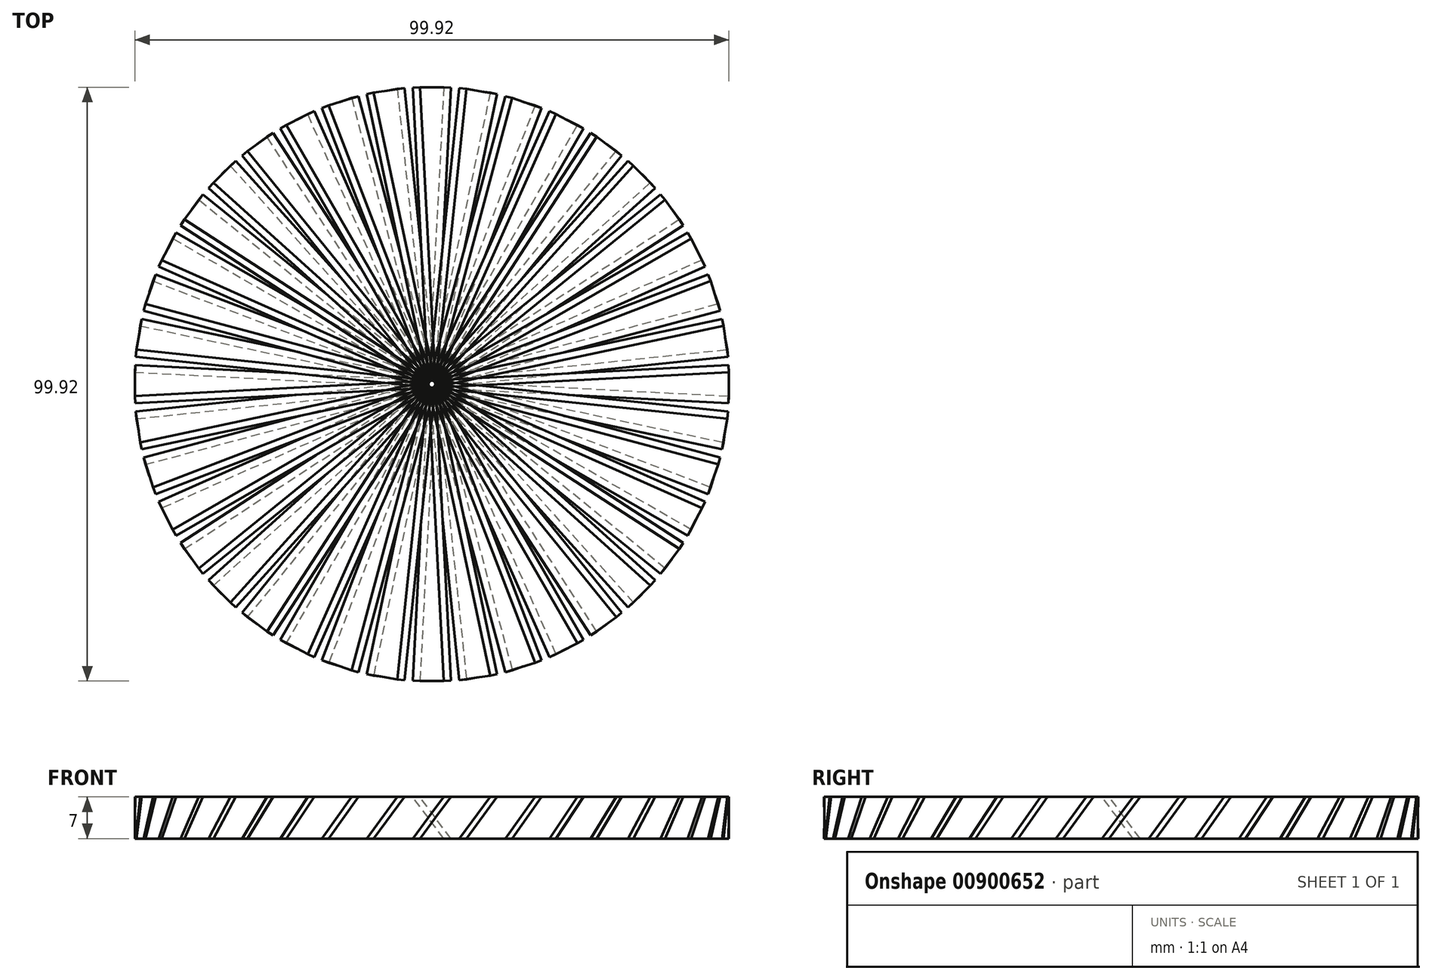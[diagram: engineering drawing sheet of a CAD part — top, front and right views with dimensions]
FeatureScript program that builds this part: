
annotation { "Feature Type Name" : "Feature", "Feature Type Description" : "" }
export const myFeature = defineFeature(function(context is Context, id is Id, definition is map)
    precondition{}
    {
        {
            var Q0;
            Q0=qCreatedBy(makeId("Top.planeOp"),FACE);
            var sketch = newSketch(context, id + "F0", { "sketchPlane" : qUnion([Q0])});
            skLineSegment(sketch, "E0.bottom", {"start": v(2.02, 49.96) * mm, "end": v(3.22, 49.9) * mm});
            skLineSegment(sketch, "E0.top", {"start": v(-3.22, -49.9) * mm, "end": v(-2.02, -49.96) * mm});
            skLineSegment(sketch, "E0.left", {"start": v(2.02, 49.96) * mm, "end": v(-3.22, -49.9) * mm});
            skLineSegment(sketch, "E0.right", {"start": v(3.22, 49.9) * mm, "end": v(-2.02, -49.96) * mm});
            skPoint(sketch, "E0.middle", {"position": v(0, 0) * mm});
            skSolve(sketch);
        }
        {
            var Q0;
            Q0=qCreatedBy(makeId("Top.planeOp"),FACE);
            cPlane(context, id + "F1", {"entities" : qUnion([Q0]), "cplaneType" : CPlaneType.OFFSET, "offset" : 7 * mm, "width" : 150 * mm, "height" : 150 * mm});
        }
        {
            var Q0;
            Q0=qCreatedBy(id+"F1.planeOp",FACE);
            var sketch = newSketch(context, id + "F2", { "sketchPlane" : qUnion([Q0])});
            skLineSegment(sketch, "E1.bottom", {"start": v(-3.22, 49.9) * mm, "end": v(-2.02, 49.96) * mm});
            skLineSegment(sketch, "E1.top", {"start": v(2.02, -49.96) * mm, "end": v(3.22, -49.9) * mm});
            skLineSegment(sketch, "E1.left", {"start": v(-3.22, 49.9) * mm, "end": v(2.02, -49.96) * mm});
            skLineSegment(sketch, "E1.right", {"start": v(-2.02, 49.96) * mm, "end": v(3.22, -49.9) * mm});
            skPoint(sketch, "E1.middle", {"position": v(0, 0) * mm});
            skSolve(sketch);
        }
        {
            var Q0;
            Q0=makeQuery(id+"F0.imprint","IMPRINT",FACE,{"disambiguationData":[TD([[makeQuery(id+"F0.imprint","IMPRINT",EDGE,{"derivedFrom":sQuery(id+"F0.wireOp",EDGE,"E0.bottom")}),-1.0]])]});
            var Q1;
            Q1=makeQuery(id+"F2.imprint","IMPRINT",FACE,{"disambiguationData":[TD([[makeQuery(id+"F2.imprint","IMPRINT",EDGE,{"derivedFrom":sQuery(id+"F2.wireOp",EDGE,"E1.bottom")}),-1.0]])]});
            loft(context, id + "F3", {"sheetProfilesArray" : [{ "sheetProfileEntities" : qUnion([Q0]) }, { "sheetProfileEntities" : qUnion([Q1]) }]});
        }
        {
            var Q0;
            Q0=qCreatedBy(makeId("Right.planeOp"),FACE);
            var sketch = newSketch(context, id + "F4", { "sketchPlane" : qUnion([Q0])});
            skLineSegment(sketch, "E2", {"start": v(0, 0) * mm, "end": v(0, 27.63) * mm});
            skSolve(sketch);
        }
        {
            var Q0;
            Q0=makeQuery(id+"F3.opLoft","SWEPT_BODY",BODY,{"disambiguationData":[OSD([makeQuery(id+"F0.imprint","IMPRINT",FACE,{"disambiguationData":[TD([[makeQuery(id+"F0.imprint","IMPRINT",EDGE,{"derivedFrom":sQuery(id+"F0.wireOp",EDGE,"E0.bottom")}),-1.0]])]}),makeQuery(id+"F2.imprint","IMPRINT",FACE,{"disambiguationData":[TD([[makeQuery(id+"F2.imprint","IMPRINT",EDGE,{"derivedFrom":sQuery(id+"F2.wireOp",EDGE,"E1.bottom")}),-1.0]])]})])]});
            var Q1;
            Q1=sQuery(id+"F4.wireOp",EDGE,"E2");
            circularPattern(context, id + "F5", {"entities" : qUnion([Q0]), "axis" : qUnion([Q1]), "angle" : 360 * degree, "instanceCount" : 40, "equalSpace" : true});
        }
    });
